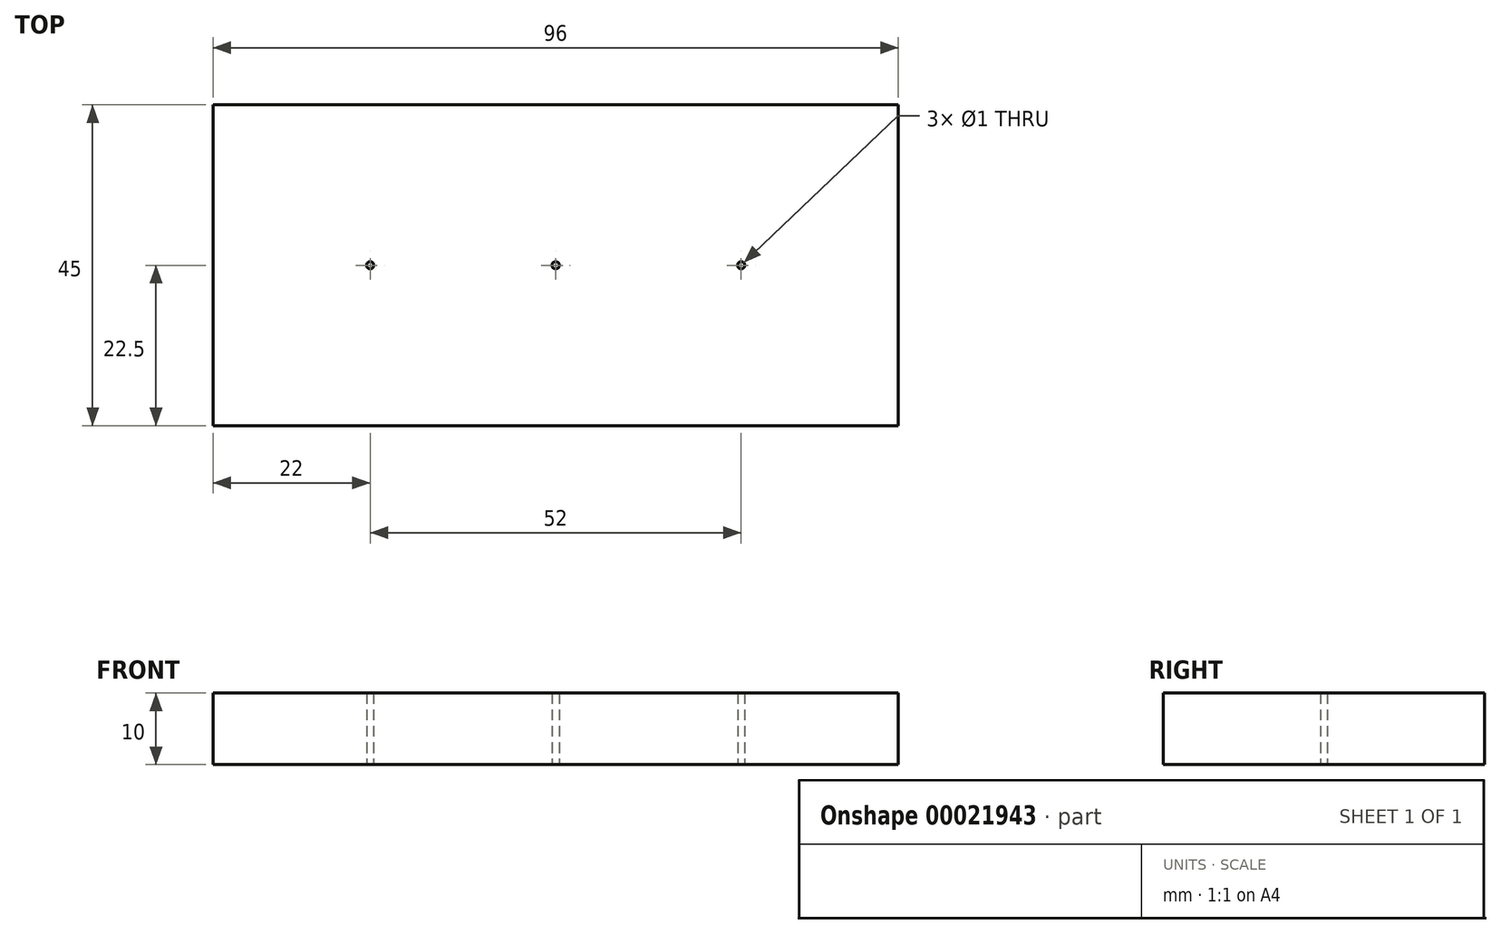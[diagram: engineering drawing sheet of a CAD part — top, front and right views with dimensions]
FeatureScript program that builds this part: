
annotation { "Feature Type Name" : "Feature", "Feature Type Description" : "" }
export const myFeature = defineFeature(function(context is Context, id is Id, definition is map)
    precondition{}
    {
        {
            var Q0;
            Q0=qCreatedBy(makeId("Top.planeOp"),FACE);
            var sketch = newSketch(context, id + "F0", { "sketchPlane" : qUnion([Q0])});
            skLineSegment(sketch, "E0.rect.bottom", {"start": v(48, -22.5) * mm, "end": v(-48, -22.5) * mm});
            skLineSegment(sketch, "E0.rect.top", {"start": v(48, 22.5) * mm, "end": v(-48, 22.5) * mm});
            skLineSegment(sketch, "E0.rect.left", {"start": v(48, -22.5) * mm, "end": v(48, 22.5) * mm});
            skLineSegment(sketch, "E0.rect.right", {"start": v(-48, -22.5) * mm, "end": v(-48, 22.5) * mm});
            skPoint(sketch, "E0.rect.middle", {"position": v(0, 0) * mm});
            skCircle(sketch, "E1", {"center": v(0, 0) * mm, "radius": 0.5 * mm});
            skCircle(sketch, "E2", {"center": v(-26, 0) * mm, "radius": 0.5 * mm});
            skCircle(sketch, "E3", {"center": v(26, 0) * mm, "radius": 0.5 * mm});
            skSolve(sketch);
        }
        {
            var Q0;
            Q0=makeQuery(id+"F0.imprint","IMPRINT",FACE,{"disambiguationData":[TD([[makeQuery(id+"F0.imprint","IMPRINT",EDGE,{"derivedFrom":sQuery(id+"F0.wireOp",EDGE,"E0.rect.bottom")}),-1.0]])]});
            extrude(context, id + "F1", {"entities" : qUnion([Q0]), "depth" : 10 * mm});
        }
    });
